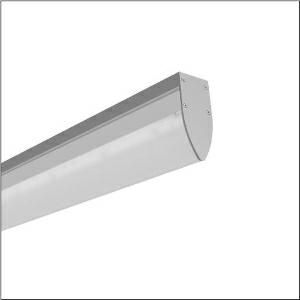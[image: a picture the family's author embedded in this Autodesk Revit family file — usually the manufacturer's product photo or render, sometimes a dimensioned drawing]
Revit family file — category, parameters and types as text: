
# Revit family: mira_r__21_td_51fr527d424a_f4a9
name_source: partatom
category: Lighting Fixtures
units: mm (PartAtom-declared; Revit-internal decimal feet)

## family parameters
Cut with Voids When Loaded = No
Host = Face
Light Source = No
Part Type = Normal
Room Calculation Point = No
Round Connector Dimension = Use Diameter
Shared = No

## types (1)
- Mira® 21 TD (1 x LED, 2020 lm, 14 W, 4000K)
    Apparent Load = 14 VA
    CIE Flux Codes = 40 68 87 81 100
    Color Rendering = 80
    Color Temperature = 4000K
    Default Elevation = 1800 mm
    Description = Mira® 21 TD, clean room luminaire, primary light control with reflector, primary optical cover: cover, of PMMA, frosted, light emission: direct distribution, primary light characteristic: symmetric, installation type: surface-mounted, LED, rated luminous flux: 2.020lm, luminous efficacy: 144lm/W, light colour: 840, colour temperature: 4000K, control gear: ECG, with terminal, 3-pole, max. 2.5mm², mains connection: 230V, AC, 50/60Hz, rated input power: 14W, luminaire housing, of sheet steel, coated, pure white, length: 600mm, width: 55mm, height: 120mm, protection rating (complete): IP43, insulation class (complete): insulation class I (protective earthing), certification: CE, UKCA, permissible operating ambient temperature: -5..+40°C, standard: EN 50419, packaging unit: 1 piece
    Height = 0 mm  [stored 0 ft]
    Lamp = 1 x LED
    Lamp Light Flux = 2020 lm
    Lamp Power = 14 W
    Lamp count = 1
    Length = 600 mm
    Luminous efficacy = 144 lm/W
    Manufacturer = Siteco
    ModVariant = No
    Model = 51FR527D424A
    Mounting Place = Ceiling
    Mounting Type = Recessed
    Number of Poles = 1
    OnlyDefault = Yes
    Power Factor = 1
    Product Name = Mira® 21 TD
    Product group = clean room luminaire
    ProductGroupID = 401
    Protection Class = Protection class I
    Protection Degree = IP 43
    RLX_Detail_Level = 1
    RlxData = <blob elided: 25833 chars, md5=9d8e7d89>
    Socket = socket
    Standby Power = 0 W
    System Light Flux = 2020 lm
    System Power = 14 W
    Type Comments = Product without accessories
    Type Image = l_1007115.jpg
    URL = http://relux.com
    VarID = ---
    Voltage = 0 V
    Weight = 0.00 kg
    Width = 55 mm

note: [stored X ft] marks values corroborated as IEEE doubles in the binary element streams (Revit-internal decimal feet)

## geometry (parser evidence)
native form markers: Blend x4, Sweep x12
no freeform markers — native parametric forms only
